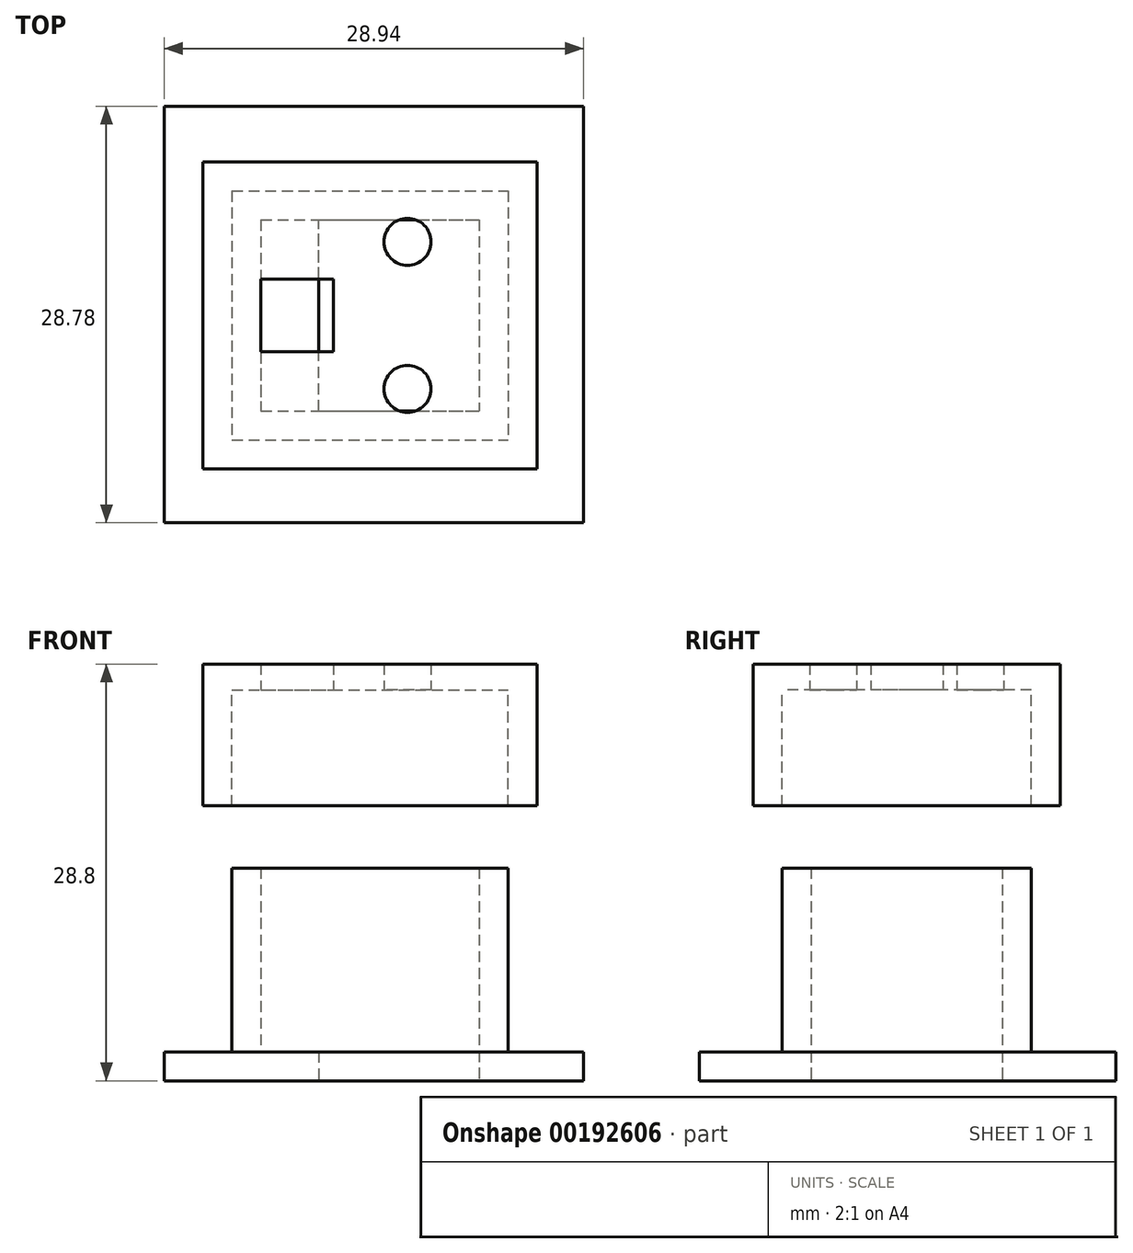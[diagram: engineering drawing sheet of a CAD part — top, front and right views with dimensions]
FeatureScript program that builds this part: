
annotation { "Feature Type Name" : "Feature", "Feature Type Description" : "" }
export const myFeature = defineFeature(function(context is Context, id is Id, definition is map)
    precondition{}
    {
        {
            var Q0;
            Q0=qCreatedBy(makeId("Top.planeOp"),FACE);
            var sketch = newSketch(context, id + "F0", { "sketchPlane" : qUnion([Q0])});
            skLineSegment(sketch, "E0.bottom", {"start": v(0, 0) * mm, "end": v(15.08, 0) * mm});
            skLineSegment(sketch, "E0.top", {"start": v(0, -13.2) * mm, "end": v(15.08, -13.2) * mm});
            skLineSegment(sketch, "E0.left", {"start": v(0, 0) * mm, "end": v(0, -13.2) * mm});
            skLineSegment(sketch, "E0.right", {"start": v(15.08, 0) * mm, "end": v(15.08, -13.2) * mm});
            skLineSegment(sketch, "E1.0", {"start": v(17.08, 2) * mm, "end": v(17.08, -15.2) * mm});
            skLineSegment(sketch, "E1.1", {"start": v(-2, 2) * mm, "end": v(17.08, 2) * mm});
            skLineSegment(sketch, "E1.2", {"start": v(-2, 2) * mm, "end": v(-2, -15.2) * mm});
            skLineSegment(sketch, "E1.3", {"start": v(-2, -15.2) * mm, "end": v(17.08, -15.2) * mm});
            skSolve(sketch);
        }
        {
            var Q0;
            Q0=makeQuery(id+"F0.imprint","IMPRINT",FACE,{"disambiguationData":[TD([[makeQuery(id+"F0.imprint","IMPRINT",EDGE,{"derivedFrom":sQuery(id+"F0.wireOp",EDGE,"E0.bottom")}),1.0]])]});
            extrude(context, id + "F1", {"entities" : qUnion([Q0]), "depth" : 12.7 * mm});
        }
        {
            var Q0;
            Q0=qCreatedBy(makeId("Top.planeOp"),FACE);
            cPlane(context, id + "F2", {"entities" : qUnion([Q0]), "cplaneType" : CPlaneType.OFFSET, "offset" : 25 * mm, "width" : 150 * mm, "height" : 150 * mm});
        }
        {
            var Q0;
            Q0=qCreatedBy(id+"F2.planeOp",FACE);
            var sketch = newSketch(context, id + "F3", { "sketchPlane" : qUnion([Q0])});
            skLineSegment(sketch, "E2.0", {"start": v(-2, 2) * mm, "end": v(17.08, 2) * mm});
            skLineSegment(sketch, "E3.0", {"start": v(17.08, 2) * mm, "end": v(17.08, -15.2) * mm});
            skLineSegment(sketch, "E4.0", {"start": v(-2, -15.2) * mm, "end": v(17.08, -15.2) * mm});
            skLineSegment(sketch, "E5.0", {"start": v(-2, 2) * mm, "end": v(-2, -15.2) * mm});
            skLineSegment(sketch, "E6.0", {"start": v(19.08, 4) * mm, "end": v(19.08, -17.21) * mm});
            skLineSegment(sketch, "E6.1", {"start": v(-4, 4) * mm, "end": v(19.08, 4) * mm});
            skLineSegment(sketch, "E6.2", {"start": v(-4, 4) * mm, "end": v(-4, -17.21) * mm});
            skLineSegment(sketch, "E6.3", {"start": v(-4, -17.21) * mm, "end": v(19.08, -17.21) * mm});
            skSolve(sketch);
        }
        {
            var Q0;
            Q0=makeQuery(id+"F3.imprint","IMPRINT",FACE,{"disambiguationData":[TD([[makeQuery(id+"F3.imprint","IMPRINT",EDGE,{"derivedFrom":sQuery(id+"F3.wireOp",EDGE,"E2.0")}),1.0]])]});
            extrude(context, id + "F4", {"entities" : qUnion([Q0]), "oppositeDirection" : true, "depth" : 8 * mm});
        }
        {
            var Q0;
            Q0=makeQuery(id+"F3.imprint","IMPRINT",FACE,{"disambiguationData":[TD([[makeQuery(id+"F3.imprint","IMPRINT",EDGE,{"derivedFrom":sQuery(id+"F3.wireOp",EDGE,"E2.0")}),-1.0]])]});
            var Q1;
            Q1=makeQuery(id+"F3.imprint","IMPRINT",FACE,{"disambiguationData":[TD([[makeQuery(id+"F3.imprint","IMPRINT",EDGE,{"derivedFrom":sQuery(id+"F3.wireOp",EDGE,"E2.0")}),1.0]])]});
            extrude(context, id + "F5", {"entities" : qUnion([Q0, Q1]), "operationType" : NewBodyOperationType.ADD, "depth" : 1.8 * mm});
        }
        {
            var Q0;
            Q0=makeQuery(id+"F3.imprint","IMPRINT",FACE,{"disambiguationData":[TD([[makeQuery(id+"F3.imprint","IMPRINT",EDGE,{"derivedFrom":sQuery(id+"F3.wireOp",EDGE,"E2.0")}),-1.0]])]});
            var sketch = newSketch(context, id + "F6", { "sketchPlane" : qUnion([Q0])});
            skLineSegment(sketch, "E7.0", {"start": v(0, -13.2) * mm, "end": v(15.08, -13.2) * mm, "construction": true});
            skLineSegment(sketch, "E8.0", {"start": v(0, 0) * mm, "end": v(0, -4.1) * mm, "construction": true});
            skLineSegment(sketch, "E9.0", {"start": v(15.08, 0) * mm, "end": v(15.08, -6.6) * mm, "construction": true});
            skLineSegment(sketch, "E10.0", {"start": v(0, 0) * mm, "end": v(15.08, 0) * mm, "construction": true});
            skPoint(sketch, "E11", {"position": v(0, -9.98) * mm});
            skPoint(sketch, "E12", {"position": v(-18.17, 13.58) * mm});
            skPoint(sketch, "E13", {"position": v(0, -4.98) * mm});
            skLineSegment(sketch, "E14", {"start": v(0, -9.1) * mm, "end": v(0, -13.2) * mm, "construction": true});
            skLineSegment(sketch, "E15", {"start": v(0, -4.1) * mm, "end": v(0, -9.1) * mm});
            skLineSegment(sketch, "E16", {"start": v(0, -9.1) * mm, "end": v(5, -9.1) * mm});
            skLineSegment(sketch, "E17", {"start": v(0, -4.1) * mm, "end": v(5, -4.1) * mm});
            skLineSegment(sketch, "E18", {"start": v(5, -4.1) * mm, "end": v(5, -9.1) * mm});
            skLineSegment(sketch, "E19", {"start": v(15.08, -6.6) * mm, "end": v(15.08, -13.2) * mm, "construction": true});
            skLineSegment(sketch, "E20", {"start": v(15.08, -6.6) * mm, "end": v(0, -6.6) * mm, "construction": true});
            skCircle(sketch, "E21", {"center": v(10.12, -11.68) * mm, "radius": 1.63 * mm});
            skCircle(sketch, "E22.MirrorC", {"center": v(10.12, -1.52) * mm, "radius": 1.63 * mm});
            skSolve(sketch);
        }
        {
            var Q0;
            Q0 = qSketchRegion(id + "F6", true);
            var Q1;
            Q1=sQuery(id+"F6.wireOp",EDGE,"E16");
            var Q2;
            Q2=sQuery(id+"F6.wireOp",EDGE,"E15");
            var Q3;
            Q3=sQuery(id+"F6.wireOp",EDGE,"E22.MirrorC");
            var Q4;
            Q4=sQuery(id+"F6.wireOp",EDGE,"E18");
            var Q5;
            Q5=sQuery(id+"F6.wireOp",EDGE,"E21");
            var Q6;
            Q6=sQuery(id+"F6.wireOp",EDGE,"E17");
            var Q7;
            Q7=makeQuery(id+"F5.opExtrude","CAP_FACE",FACE,{"disambiguationData":[OSD([sQuery(id+"F3.wireOp",EDGE,"E6.0"),sQuery(id+"F3.wireOp",EDGE,"E6.1"),sQuery(id+"F3.wireOp",EDGE,"E6.2"),sQuery(id+"F3.wireOp",EDGE,"E6.3")])],"isStart":false});
            extrude(context, id + "F7", {"entities" : qUnion([Q0]), "operationType" : NewBodyOperationType.REMOVE, "surfaceEntities" : qUnion([Q1, Q2, Q3, Q4, Q5, Q6]), "endBound" : BoundingType.UP_TO_SURFACE, "endBoundEntityFace" : qUnion([Q7]), "depth" : 25 * mm});
        }
        {
            var Q0;
            Q0=qCreatedBy(makeId("Top.planeOp"),FACE);
            var sketch = newSketch(context, id + "F8", { "sketchPlane" : qUnion([Q0])});
            skLineSegment(sketch, "E23.bottom", {"start": v(22.27, 7.84) * mm, "end": v(-6.67, 7.84) * mm});
            skLineSegment(sketch, "E23.top", {"start": v(22.27, -20.94) * mm, "end": v(-6.67, -20.94) * mm});
            skLineSegment(sketch, "E23.left", {"start": v(22.27, 7.84) * mm, "end": v(22.27, -20.94) * mm});
            skLineSegment(sketch, "E23.right", {"start": v(-6.67, 7.84) * mm, "end": v(-6.67, -20.94) * mm});
            skSolve(sketch);
        }
        {
            var Q0;
            Q0=makeQuery(id+"F8.imprint","IMPRINT",FACE,{"disambiguationData":[TD([[makeQuery(id+"F8.imprint","IMPRINT",EDGE,{"derivedFrom":sQuery(id+"F8.wireOp",EDGE,"E23.bottom")}),1.0]])]});
            extrude(context, id + "F9", {"entities" : qUnion([Q0]), "operationType" : NewBodyOperationType.ADD, "oppositeDirection" : true, "depth" : 2 * mm});
        }
        {
            var Q0;
            Q0=makeQuery(id+"F9.opExtrude","CAP_FACE",FACE,{"disambiguationData":[OSD([sQuery(id+"F8.wireOp",EDGE,"E23.bottom"),sQuery(id+"F8.wireOp",EDGE,"E23.top"),sQuery(id+"F8.wireOp",EDGE,"E23.left"),sQuery(id+"F8.wireOp",EDGE,"E23.right")])],"isStart":false});
            var sketch = newSketch(context, id + "F10", { "sketchPlane" : qUnion([Q0])});
            skSolve(sketch);
        }
        {
            var Q0;
            Q0=makeQuery(id+"F10.imprint","IMPRINT",FACE,{"disambiguationData":[TD([[makeQuery(id+"F10.imprint","IMPRINT",EDGE,{"derivedFrom":makeQuery(id+"F9.opExtrude","CAP_EDGE",EDGE,{"disambiguationData":[OSD([sQuery(id+"F8.wireOp",EDGE,"E23.bottom")])],"isStart":false})}),-1.0]])]});
            var sketch = newSketch(context, id + "F11", { "sketchPlane" : qUnion([Q0])});
            skLineSegment(sketch, "E24.0", {"start": v(15.08, 0) * mm, "end": v(15.08, 13.2) * mm});
            skLineSegment(sketch, "E25", {"start": v(4, 13.2) * mm, "end": v(15.08, 13.2) * mm});
            skLineSegment(sketch, "E26", {"start": v(4, 0) * mm, "end": v(15.08, 0) * mm});
            skLineSegment(sketch, "E27", {"start": v(4, 13.2) * mm, "end": v(4, 0) * mm});
            skSolve(sketch);
        }
        {
            var Q0;
            Q0 = qSketchRegion(id + "F11", true);
            var Q1;
            {var subQ0=sQuery(id+"F8.wireOp",EDGE,"E23.right");var subQ1=sQuery(id+"F8.wireOp",EDGE,"E23.bottom");var subQ2=sQuery(id+"F8.wireOp",EDGE,"E23.top");var subQ3=sQuery(id+"F8.wireOp",EDGE,"E23.left");Q1=makeQuery(id+"F9.boolean.opBoolean","SPLIT",FACE,{"disambiguationData":[TD([makeQuery(id+"F1.opExtrude","SWEPT_FACE",FACE,{"disambiguationData":[OSD([sQuery(id+"F0.wireOp",EDGE,"E1.0")])]})])],"derivedFrom":makeQuery(id+"F9.opExtrude","CAP_FACE",FACE,{"disambiguationData":[OSD([subQ1,subQ2,subQ3,subQ0])],"isStart":true})});}
            extrude(context, id + "F12", {"entities" : qUnion([Q0]), "operationType" : NewBodyOperationType.REMOVE, "endBound" : BoundingType.UP_TO_SURFACE, "oppositeDirection" : true, "endBoundEntityFace" : qUnion([Q1]), "depth" : 25 * mm});
        }
    });
